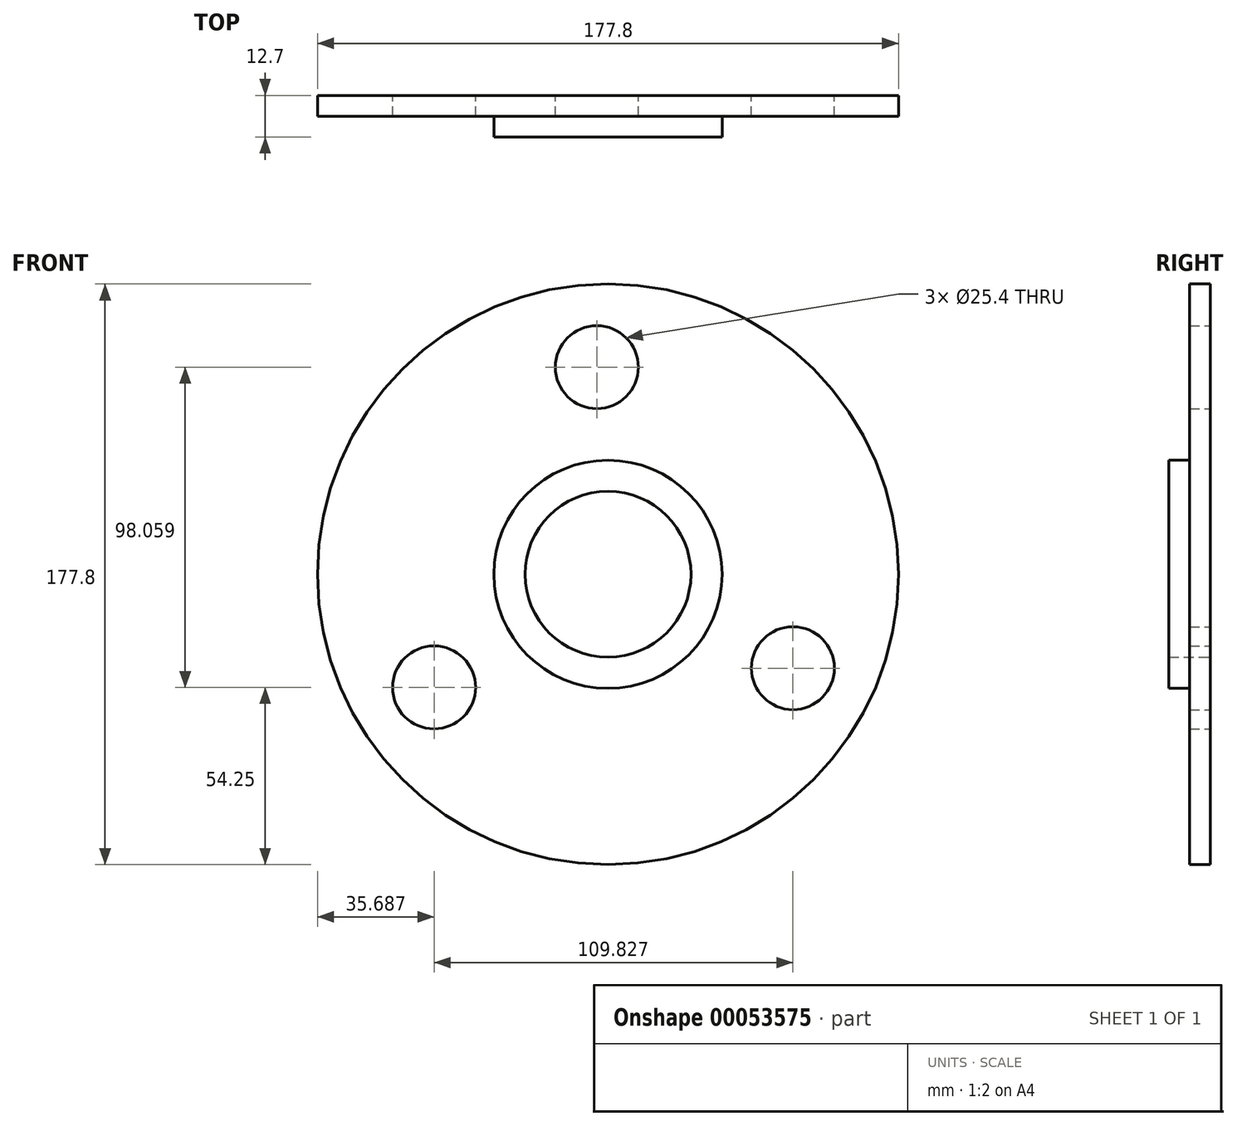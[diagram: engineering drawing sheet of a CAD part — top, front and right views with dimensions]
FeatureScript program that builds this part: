
annotation { "Feature Type Name" : "Feature", "Feature Type Description" : "" }
export const myFeature = defineFeature(function(context is Context, id is Id, definition is map)
    precondition{}
    {
        {
            var Q0;
            Q0=qCreatedBy(makeId("Front.planeOp"),FACE);
            var sketch = newSketch(context, id + "F0", { "sketchPlane" : qUnion([Q0])});
            skCircle(sketch, "E0", {"center": v(0, 0) * mm, "radius": 88.9 * mm});
            skCircle(sketch, "E1", {"center": v(0, 0) * mm, "radius": 63.5 * mm, "construction": true});
            skCircle(sketch, "E2", {"center": v(0, 0) * mm, "radius": 25.4 * mm});
            skCircle(sketch, "E3", {"center": v(0, 0) * mm, "radius": 34.93 * mm});
            skCircle(sketch, "E4", {"center": v(-3.4, 63.4) * mm, "radius": 12.7 * mm});
            skCircle(sketch, "E5.1.0", {"center": v(-53.21, -34.65) * mm, "radius": 12.7 * mm});
            skCircle(sketch, "E5.2.0", {"center": v(56.61, -28.76) * mm, "radius": 12.7 * mm});
            skSolve(sketch);
        }
        {
            var Q0;
            Q0 = qSketchRegion(id + "F0", true);
            var Q1;
            Q1=makeQuery(id+"F0.imprint","IMPRINT",FACE,{"disambiguationData":[TD([[makeQuery(id+"F0.imprint","IMPRINT",EDGE,{"derivedFrom":sQuery(id+"F0.wireOp",EDGE,"E0")}),1.0]])]});
            extrude(context, id + "F1", {"entities" : qUnion([Q0, Q1]), "depth" : 6.35 * mm});
        }
        {
            var Q0;
            Q0=makeQuery(id+"F0.imprint","IMPRINT",FACE,{"disambiguationData":[TD([[makeQuery(id+"F0.imprint","IMPRINT",EDGE,{"derivedFrom":sQuery(id+"F0.wireOp",EDGE,"E2")}),-1.0]])]});
            extrude(context, id + "F2", {"entities" : qUnion([Q0]), "operationType" : NewBodyOperationType.ADD, "depth" : 12.7 * mm});
        }
    });
